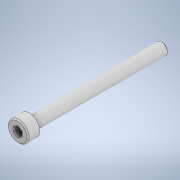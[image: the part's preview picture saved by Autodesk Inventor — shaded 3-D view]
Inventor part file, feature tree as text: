
AUTODESK INVENTOR PART (.ipt)
format: ipt  version: 2020 (Build 240168000, 168)  size: 133,120 bytes
history: native  units: mm
features: sketch x6, extrude x3, chamfer x2, other x1, fillet x1
ambient origin geometry x8: Origin, YZ Plane, XZ Plane, XY Plane, X Axis, Y Axis, Z Axis, Center Point
bodies: Body1 (feature_tree)
feature tree (13):
  other  "Bryła1"
  extrude  "Wyciągnięcie proste1"  Depth=7.0mm
  chamfer  "Faza1"  Distance=4.0mm
  sketch  "Szkic2"
  extrude  "Wyciągnięcie proste2"  Depth=2.0mm TaperAngle=45.0deg
  extrude  "Wyciągnięcie proste3"  Depth=3.071mm
  fillet  "Zaokrąglenie1"  Radius=2.0mm
  sketch  "Szkic5"
  chamfer  "Faza2"  Distance=4.0mm
  sketch  "Szkic6"
  sketch  "Szkic1"
  sketch  "Szkic3"
  sketch  "Szkic4"
